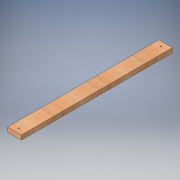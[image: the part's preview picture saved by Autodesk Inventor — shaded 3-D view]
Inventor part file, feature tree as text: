
AUTODESK INVENTOR PART (.ipt)
format: ipt  version: 2016 (Build 200138000, 138)  size: 123,392 bytes
history: native  units: in
note: dims shown in document units (in); Inventor stores cm internally (conversion verified against a paired STEP export)
features: sketch x2, extrude x1, hole x1
ambient origin geometry x8: Origin, YZ Plane, XZ Plane, XY Plane, X Axis, Y Axis, Z Axis, Center Point
bodies: Solid1 (feature_tree)
feature tree (4):
  extrude  "Extrusion1"  Depth=33.0in
  hole  "Hole1"  [1 undecoded]
  sketch  "Sketch1"  dims[d0=3.0in d1=33.0in]
  sketch  "Sketch2"  dims[d2=1.0in d3=0.0in d4=31.0in d5=15.5in d6=0.25in d7=0.75in d8=0.375in d9=0.25in d10=0.5635in d11=1.0in d12=0.8108in]
note: 1 required parameter value undecoded (feature->parameter linkage not recoverable at this tier; creation-order binding heuristic only, values carry confidence <= 0.55)
